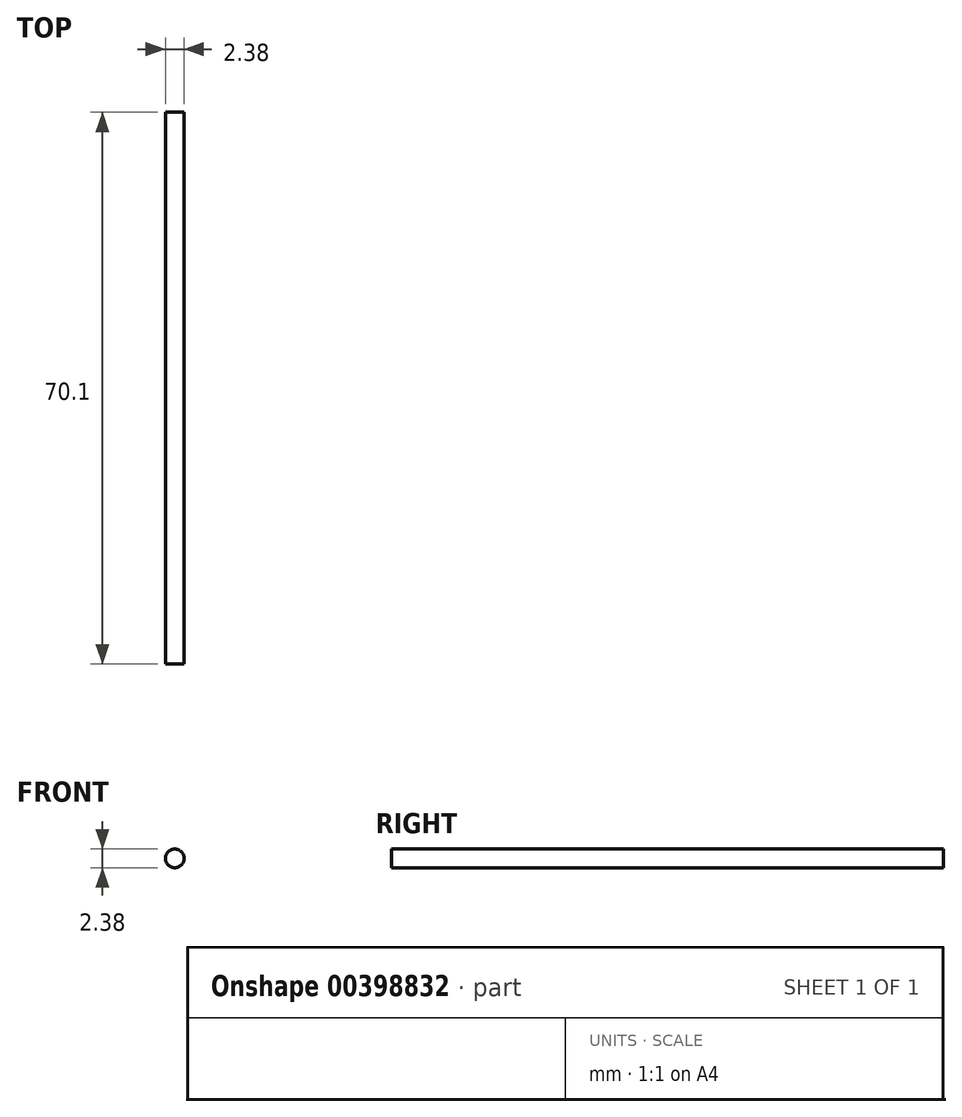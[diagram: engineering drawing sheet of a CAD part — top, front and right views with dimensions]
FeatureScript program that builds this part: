
annotation { "Feature Type Name" : "Feature", "Feature Type Description" : "" }
export const myFeature = defineFeature(function(context is Context, id is Id, definition is map)
    precondition{}
    {
        {
            var Q0;
            Q0=qCreatedBy(makeId("Front.planeOp"),FACE);
            var sketch = newSketch(context, id + "F0", { "sketchPlane" : qUnion([Q0])});
            skCircle(sketch, "E0", {"center": v(0, 0) * mm, "radius": 1.19 * mm});
            skSolve(sketch);
        }
        {
            var Q0;
            Q0 = qSketchRegion(id + "F0", true);
            extrude(context, id + "F1", {"entities" : qUnion([Q0]), "offsetDistance" : 25.4 * mm, "depth" : 70.1 * mm});
        }
    });
